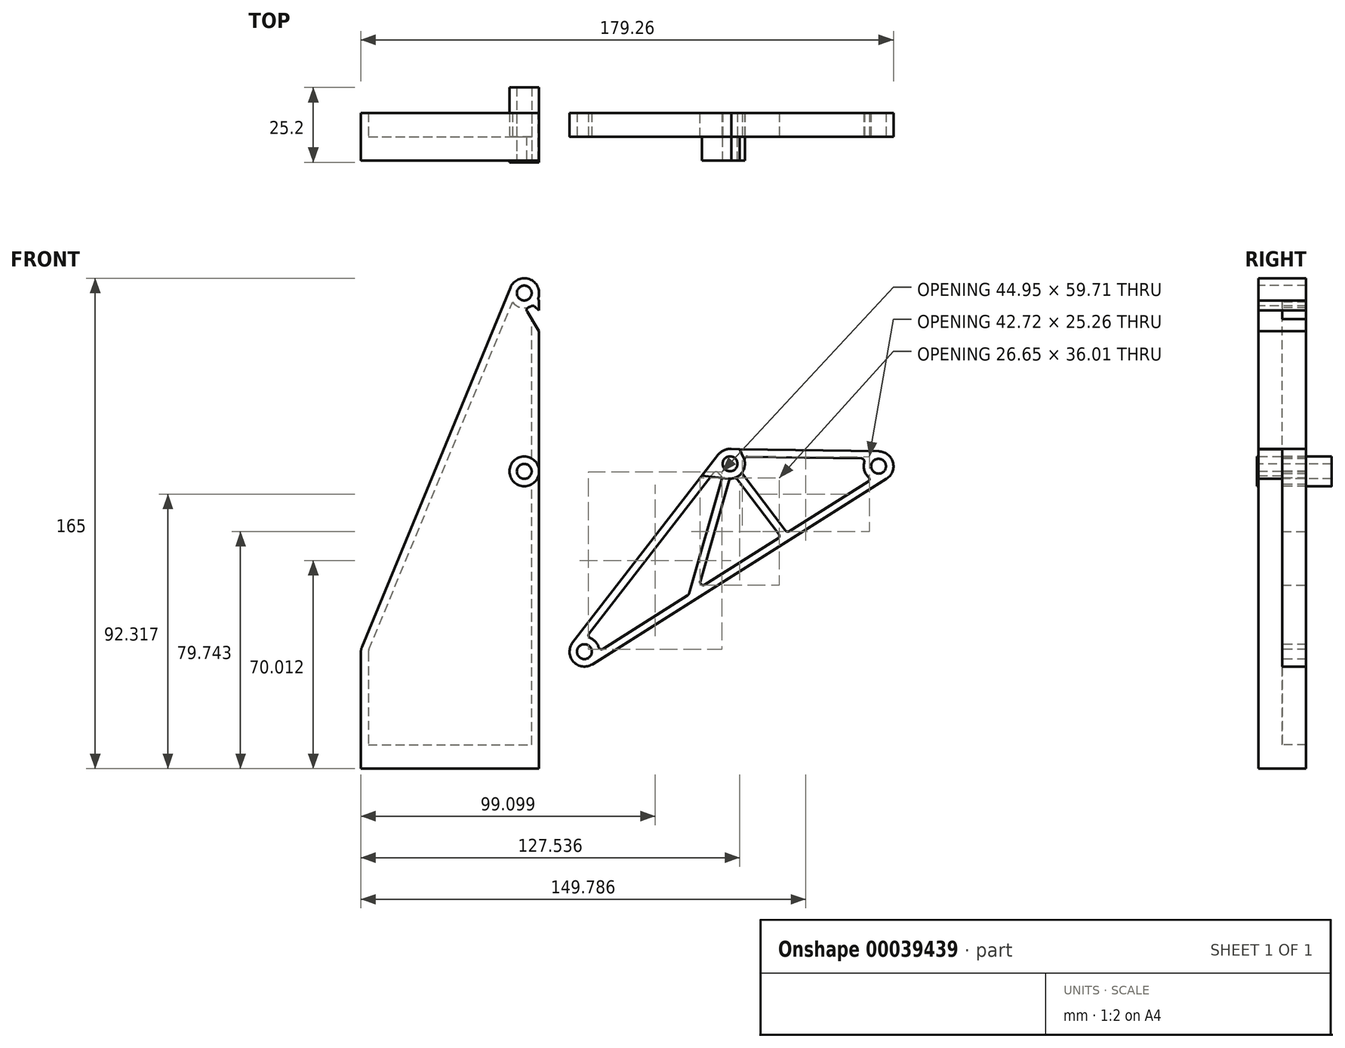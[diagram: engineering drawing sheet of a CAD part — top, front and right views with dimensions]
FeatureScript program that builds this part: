
annotation { "Feature Type Name" : "Feature", "Feature Type Description" : "" }
export const myFeature = defineFeature(function(context is Context, id is Id, definition is map)
    precondition{}
    {
        {
            var Q0;
            Q0=qCreatedBy(makeId("Front.planeOp"),FACE);
            var sketch = newSketch(context, id + "F0", { "sketchPlane" : qUnion([Q0])});
            skLineSegment(sketch, "E0", {"start": v(0, 0) * mm, "end": v(-60, 0) * mm});
            skLineSegment(sketch, "E1", {"start": v(0, 160) * mm, "end": v(0, 0) * mm});
            skCircle(sketch, "E2", {"center": v(-5, 100) * mm, "radius": 2.5 * mm});
            skCircle(sketch, "E3", {"center": v(-5, 160) * mm, "radius": 2.5 * mm});
            skArc(sketch, "E4", {"start": v(0, 160) * mm, "mid": v(-6.37, 164.8) * mm, "end": v(-9.25, 157.36) * mm});
            skLineSegment(sketch, "E5", {"start": v(-5, 160) * mm, "end": v(64.27, 102.54) * mm, "construction": true});
            skLineSegment(sketch, "E6", {"start": v(64.27, 102.54) * mm, "end": v(15.25, 39.32) * mm, "construction": true});
            skLineSegment(sketch, "E7", {"start": v(14.24, 144.04) * mm, "end": v(33.4, 167.13) * mm, "construction": true});
            skLineSegment(sketch, "E8", {"start": v(41.18, 121.7) * mm, "end": v(28.41, 106.3) * mm, "construction": true});
            skLineSegment(sketch, "E9", {"start": v(82.65, 126.25) * mm, "end": v(114.26, 101.74) * mm, "construction": true});
            skLineSegment(sketch, "E10", {"start": v(64.27, 102.54) * mm, "end": v(82.65, 126.25) * mm, "construction": true});
            skArc(sketch, "E11", {"start": v(11.3, 42.38) * mm, "mid": v(11.54, 35.96) * mm, "end": v(17.91, 35.1) * mm});
            skArc(sketch, "E12", {"start": v(116.93, 97.5) * mm, "mid": v(119.08, 103.08) * mm, "end": v(114.34, 106.74) * mm});
            skArc(sketch, "E13", {"start": v(64.35, 107.54) * mm, "mid": v(62.1, 107.05) * mm, "end": v(60.32, 105.6) * mm});
            skLineSegment(sketch, "E14", {"start": v(17.91, 35.1) * mm, "end": v(116.93, 97.5) * mm});
            skLineSegment(sketch, "E15", {"start": v(114.34, 106.74) * mm, "end": v(64.35, 107.54) * mm});
            skLineSegment(sketch, "E16", {"start": v(11.3, 42.38) * mm, "end": v(60.32, 105.6) * mm});
            skArc(sketch, "E17", {"start": v(-5.91, 164.92) * mm, "mid": v(-9.57, 162.02) * mm, "end": v(-9.25, 157.36) * mm});
            skArc(sketch, "E18", {"start": v(37.9, 169.29) * mm, "mid": v(35.66, 171.59) * mm, "end": v(32.48, 172.04) * mm});
            skArc(sketch, "E19", {"start": v(63.75, 97.57) * mm, "mid": v(68.35, 99.66) * mm, "end": v(68.78, 104.7) * mm});
            skArc(sketch, "E20", {"start": v(24.17, 103.66) * mm, "mid": v(25.76, 102.06) * mm, "end": v(27.89, 101.33) * mm});
            skLineSegment(sketch, "E21", {"start": v(24.17, 103.66) * mm, "end": v(-9.25, 157.36) * mm});
            skLineSegment(sketch, "E22", {"start": v(-5.91, 164.92) * mm, "end": v(32.48, 172.04) * mm});
            skLineSegment(sketch, "E23", {"start": v(37.9, 169.29) * mm, "end": v(68.78, 104.7) * mm});
            skLineSegment(sketch, "E24", {"start": v(63.75, 97.57) * mm, "end": v(27.89, 101.33) * mm});
            skCircle(sketch, "E25", {"center": v(33.4, 167.13) * mm, "radius": 2.5 * mm});
            skCircle(sketch, "E26", {"center": v(64.27, 102.54) * mm, "radius": 2.5 * mm});
            skCircle(sketch, "E27", {"center": v(114.26, 101.74) * mm, "radius": 2.5 * mm});
            skCircle(sketch, "E28", {"center": v(15.25, 39.32) * mm, "radius": 2.5 * mm});
            skLineSegment(sketch, "E29", {"start": v(-60, 0) * mm, "end": v(-60, 39) * mm});
            skLineSegment(sketch, "E30", {"start": v(-59.62, 40.92) * mm, "end": v(-9.62, 161.9) * mm});
            skPoint(sketch, "E31.visualSharp", {"position": v(-60, 40) * mm});
            skArc(sketch, "E31.filletArc", {"start": v(-59.62, 40.92) * mm, "mid": v(-59.9, 39.98) * mm, "end": v(-60, 39) * mm});
            skCircle(sketch, "E32", {"center": v(28.41, 106.3) * mm, "radius": 2.5 * mm});
            skPoint(sketch, "E33.endSnap0", {"position": v(-6.37, 164.8) * mm});
            skSolve(sketch);
        }
        {
            var Q0;
            Q0=makeQuery(id+"F0.imprint","IMPRINT",FACE,{"disambiguationData":[TD([[makeQuery(id+"F0.imprint","IMPRINT",EDGE,{"derivedFrom":sQuery(id+"F0.wireOp",EDGE,"E0")}),-1.0]])]});
            var Q1;
            Q1=makeQuery(id+"F0.imprint","IMPRINT",FACE,{"disambiguationData":[TD([[makeQuery(id+"F0.imprint","IMPRINT",EDGE,{"derivedFrom":sQuery(id+"F0.wireOp",EDGE,"E3")}),-1.0]])]});
            extrude(context, id + "F1", {"entities" : qUnion([Q0, Q1]), "oppositeDirection" : true, "depth" : 8 * mm});
        }
        {
            var Q0;
            {var subQ7=sQuery(id+"F0.wireOp",EDGE,"E4");Q0=makeQuery(id+"F0.imprint","IMPRINT",FACE,{"disambiguationData":[TD([[makeQuery(id+"F0.imprint","IMPRINT",EDGE,{"derivedFrom":subQ7}),-1.0]])]});}
            var Q1;
            {var subQ4=sQuery(id+"F0.wireOp",EDGE,"E13");Q1=makeQuery(id+"F0.imprint","IMPRINT",FACE,{"disambiguationData":[TD([[makeQuery(id+"F0.imprint","IMPRINT",EDGE,{"derivedFrom":subQ4}),1.0]])]});}
            var Q2;
            Q2=makeQuery(id+"F0.imprint","IMPRINT",FACE,{"disambiguationData":[TD([[makeQuery(id+"F0.imprint","IMPRINT",EDGE,{"derivedFrom":sQuery(id+"F0.wireOp",EDGE,"E3")}),-1.0]])]});
            extrude(context, id + "F2", {"entities" : qUnion([Q0, Q1, Q2]), "depth" : 8 * mm});
        }
        {
            var Q0;
            {var subQ3=sQuery(id+"F0.wireOp",EDGE,"E11");Q0=makeQuery(id+"F0.imprint","IMPRINT",FACE,{"disambiguationData":[TD([[makeQuery(id+"F0.imprint","IMPRINT",EDGE,{"derivedFrom":subQ3}),1.0]])]});}
            var Q1;
            {var subQ4=sQuery(id+"F0.wireOp",EDGE,"E13");Q1=makeQuery(id+"F0.imprint","IMPRINT",FACE,{"disambiguationData":[TD([[makeQuery(id+"F0.imprint","IMPRINT",EDGE,{"derivedFrom":subQ4}),1.0]])]});}
            var Q2;
            {var subQ0=sQuery(id+"F0.wireOp",EDGE,"E12");Q2=makeQuery(id+"F0.imprint","IMPRINT",FACE,{"disambiguationData":[TD([[makeQuery(id+"F0.imprint","IMPRINT",EDGE,{"derivedFrom":subQ0}),1.0]])]});}
            extrude(context, id + "F3", {"entities" : qUnion([Q0, Q1, Q2]), "oppositeDirection" : true, "depth" : 8 * mm});
        }
        {
            var Q0;
            Q0=makeQuery(id+"F3.opExtrude","CAP_FACE",FACE,{"disambiguationData":[OSD([sQuery(id+"F0.wireOp",EDGE,"E11"),sQuery(id+"F0.wireOp",EDGE,"E12"),sQuery(id+"F0.wireOp",EDGE,"E13"),sQuery(id+"F0.wireOp",EDGE,"E14"),sQuery(id+"F0.wireOp",EDGE,"E15"),sQuery(id+"F0.wireOp",EDGE,"E16"),sQuery(id+"F0.wireOp",EDGE,"E26"),sQuery(id+"F0.wireOp",EDGE,"E27"),sQuery(id+"F0.wireOp",EDGE,"E28")])],"isStart":true});
            var sketch = newSketch(context, id + "F4", { "sketchPlane" : qUnion([Q0])});
            skLineSegment(sketch, "E34.0", {"start": v(13.27, 40.85) * mm, "end": v(15.92, 44.27) * mm});
            skLineSegment(sketch, "E35.0", {"start": v(114.3, 104.24) * mm, "end": v(64.31, 105.04) * mm});
            skLineSegment(sketch, "E36.0", {"start": v(16.58, 37.2) * mm, "end": v(20.24, 39.51) * mm});
            skCircle(sketch, "E37", {"center": v(114.26, 101.74) * mm, "radius": 2.5 * mm});
            skCircle(sketch, "E38", {"center": v(15.25, 39.32) * mm, "radius": 2.5 * mm});
            skArc(sketch, "E39", {"start": v(20.24, 39.51) * mm, "mid": v(18.95, 42.68) * mm, "end": v(15.92, 44.27) * mm});
            skLineSegment(sketch, "E40.trimOffspring", {"start": v(20.24, 39.51) * mm, "end": v(115.6, 99.62) * mm});
            skLineSegment(sketch, "E41.trimOffspring", {"start": v(15.92, 44.27) * mm, "end": v(62.3, 104.07) * mm});
            skCircle(sketch, "E42", {"center": v(114.26, 101.74) * mm, "radius": 5 * mm});
            skCircle(sketch, "E43", {"center": v(64.27, 102.54) * mm, "radius": 5 * mm});
            skLineSegment(sketch, "E44", {"start": v(64.27, 102.54) * mm, "end": v(50.9, 55.89) * mm, "construction": true});
            skLineSegment(sketch, "E45", {"start": v(64.27, 102.54) * mm, "end": v(83.9, 76.68) * mm, "construction": true});
            skLineSegment(sketch, "E46", {"start": v(115.6, 99.62) * mm, "end": v(116.93, 97.5) * mm, "construction": true});
            skLineSegment(sketch, "E47.0", {"start": v(63.07, 102.88) * mm, "end": v(49.7, 56.23) * mm});
            skLineSegment(sketch, "E48.0", {"start": v(65.47, 102.2) * mm, "end": v(52.1, 55.54) * mm});
            skLineSegment(sketch, "E49.0", {"start": v(63.27, 101.78) * mm, "end": v(82.9, 75.93) * mm});
            skLineSegment(sketch, "E50.0", {"start": v(65.27, 103.3) * mm, "end": v(84.9, 77.44) * mm});
            skSolve(sketch);
        }
        {
            var Q0;
            {var subQ8=sQuery(id+"F4.wireOp",EDGE,"e6ad8ed1-898a-40d8-b4cc-a0c7f3deb401");Q0=makeQuery(id+"F4.imprint","IMPRINT",FACE,{"disambiguationData":[TD([[makeQuery(id+"F4.imprint","IMPRINT",EDGE,{"derivedFrom":subQ8}),-1.0]])]});}
            var Q1;
            {var subQ4=sQuery(id+"F4.wireOp",EDGE,"71649f5b-346c-4b52-ad70-852c755155e4");Q1=makeQuery(id+"F4.imprint","IMPRINT",FACE,{"disambiguationData":[TD([[makeQuery(id+"F4.imprint","IMPRINT",EDGE,{"derivedFrom":subQ4}),1.0]])]});}
            var Q2;
            {var subQ5=sQuery(id+"F4.wireOp",EDGE,"E39");Q2=makeQuery(id+"F4.imprint","IMPRINT",FACE,{"disambiguationData":[TD([[makeQuery(id+"F4.imprint","IMPRINT",EDGE,{"derivedFrom":subQ5}),-1.0]])]});}
            var Q3;
            {var subQ7=sQuery(id+"F4.wireOp",EDGE,"cc853d74-6e0b-4ffd-9b44-5db66f43a1f3");Q3=makeQuery(id+"F4.imprint","IMPRINT",FACE,{"disambiguationData":[TD([[makeQuery(id+"F4.imprint","IMPRINT",EDGE,{"derivedFrom":subQ7}),1.0]])]});}
            var Q4;
            {var subQ3=sQuery(id+"F4.wireOp",EDGE,"E40.trimOffspring");var subQ5=sQuery(id+"F4.wireOp",EDGE,"E48.0");var subQ7=makeQuery(id+"F4.imprint","INTERSECT",VERTEX,{"derivedFrom":[subQ3,subQ5]});Q4=makeQuery(id+"F4.imprint","IMPRINT",FACE,{"disambiguationData":[TD([[makeQuery(id+"F4.imprint","IMPRINT",EDGE,{"disambiguationData":[TD([[subQ7,-1.0]])],"derivedFrom":subQ3}),1.0]])]});}
            var Q5;
            {var subQ5=sQuery(id+"F4.wireOp",EDGE,"E35.0");var subQ7=sQuery(id+"F4.wireOp",EDGE,"E42");var subQ8=makeQuery(id+"F4.imprint","INTERSECT",VERTEX,{"derivedFrom":[subQ5,subQ7]});Q5=makeQuery(id+"F4.imprint","IMPRINT",FACE,{"disambiguationData":[TD([[makeQuery(id+"F4.imprint","IMPRINT",EDGE,{"disambiguationData":[TD([[subQ8,-1.0]])],"derivedFrom":subQ5}),1.0]])]});}
            extrude(context, id + "F5", {"entities" : qUnion([Q0, Q1, Q2, Q3, Q4, Q5]), "operationType" : NewBodyOperationType.REMOVE, "endBound" : BoundingType.THROUGH_ALL, "oppositeDirection" : true, "depth" : 25 * mm});
        }
        {
            var Q0;
            Q0=makeQuery(id+"F2.opExtrude","CAP_FACE",FACE,{"disambiguationData":[OSD([sQuery(id+"F0.wireOp",EDGE,"E3"),sQuery(id+"F0.wireOp",EDGE,"E17"),sQuery(id+"F0.wireOp",EDGE,"E18"),sQuery(id+"F0.wireOp",EDGE,"E19"),sQuery(id+"F0.wireOp",EDGE,"E20"),sQuery(id+"F0.wireOp",EDGE,"E21"),sQuery(id+"F0.wireOp",EDGE,"E22"),sQuery(id+"F0.wireOp",EDGE,"E23"),sQuery(id+"F0.wireOp",EDGE,"E24"),sQuery(id+"F0.wireOp",EDGE,"E25"),sQuery(id+"F0.wireOp",EDGE,"E26"),sQuery(id+"F0.wireOp",EDGE,"E32")])],"isStart":false});
            var sketch = newSketch(context, id + "F6", { "sketchPlane" : qUnion([Q0])});
            skLineSegment(sketch, "E51", {"start": v(28.41, 106.3) * mm, "end": v(33.4, 167.13) * mm, "construction": true});
            skLineSegment(sketch, "E52", {"start": v(-5, 160) * mm, "end": v(64.27, 102.54) * mm, "construction": true});
            skLineSegment(sketch, "E53.0", {"start": v(-5.46, 162.46) * mm, "end": v(32.94, 169.59) * mm});
            skLineSegment(sketch, "E54", {"start": v(-7.12, 158.68) * mm, "end": v(26.29, 104.98) * mm});
            skLineSegment(sketch, "E55", {"start": v(28.15, 103.81) * mm, "end": v(64, 100.05) * mm});
            skLineSegment(sketch, "E56", {"start": v(66.53, 103.62) * mm, "end": v(35.65, 168.2) * mm});
            skCircle(sketch, "E57", {"center": v(-5, 160) * mm, "radius": 5 * mm});
            skCircle(sketch, "E58", {"center": v(33.4, 167.13) * mm, "radius": 5 * mm});
            skCircle(sketch, "E59", {"center": v(64.27, 102.54) * mm, "radius": 5 * mm});
            skCircle(sketch, "E60", {"center": v(28.41, 106.3) * mm, "radius": 5 * mm});
            skLineSegment(sketch, "E61.0", {"start": v(29.66, 106.2) * mm, "end": v(34.64, 167.03) * mm});
            skLineSegment(sketch, "E62.0", {"start": v(27.17, 106.4) * mm, "end": v(32.15, 167.23) * mm});
            skLineSegment(sketch, "E63.0", {"start": v(-5.8, 159.04) * mm, "end": v(63.47, 101.58) * mm});
            skLineSegment(sketch, "E64.0", {"start": v(-4.2, 160.96) * mm, "end": v(65.07, 103.5) * mm});
            skSolve(sketch);
        }
        {
            var Q0;
            {var subQ3=sQuery(id+"F6.wireOp",EDGE,"E57");var subQ7=sQuery(id+"F6.wireOp",EDGE,"E54");var subQ9=makeQuery(id+"F6.imprint","INTERSECT",VERTEX,{"derivedFrom":[subQ7,subQ3]});Q0=makeQuery(id+"F6.imprint","IMPRINT",FACE,{"disambiguationData":[TD([[makeQuery(id+"F6.imprint","IMPRINT",EDGE,{"disambiguationData":[TD([[subQ9,-1.0]])],"derivedFrom":subQ7}),1.0]])]});}
            var Q1;
            {var subQ3=sQuery(id+"F6.wireOp",EDGE,"E57");var subQ5=sQuery(id+"F6.wireOp",EDGE,"E53.0");var subQ8=makeQuery(id+"F6.imprint","INTERSECT",VERTEX,{"derivedFrom":[subQ5,subQ3]});Q1=makeQuery(id+"F6.imprint","IMPRINT",FACE,{"disambiguationData":[TD([[makeQuery(id+"F6.imprint","IMPRINT",EDGE,{"disambiguationData":[TD([[subQ8,-1.0]])],"derivedFrom":subQ5}),-1.0]])]});}
            var Q2;
            {var subQ3=sQuery(id+"F6.wireOp",EDGE,"E59");var subQ5=sQuery(id+"F6.wireOp",EDGE,"E56");var subQ8=makeQuery(id+"F6.imprint","INTERSECT",VERTEX,{"derivedFrom":[subQ5,subQ3]});Q2=makeQuery(id+"F6.imprint","IMPRINT",FACE,{"disambiguationData":[TD([[makeQuery(id+"F6.imprint","IMPRINT",EDGE,{"disambiguationData":[TD([[subQ8,-1.0]])],"derivedFrom":subQ5}),1.0]])]});}
            var Q3;
            {var subQ5=sQuery(id+"F6.wireOp",EDGE,"E60");var subQ7=sQuery(id+"F6.wireOp",EDGE,"E55");var subQ8=makeQuery(id+"F6.imprint","INTERSECT",VERTEX,{"derivedFrom":[subQ7,subQ5]});Q3=makeQuery(id+"F6.imprint","IMPRINT",FACE,{"disambiguationData":[TD([[makeQuery(id+"F6.imprint","IMPRINT",EDGE,{"disambiguationData":[TD([[subQ8,-1.0]])],"derivedFrom":subQ7}),1.0]])]});}
            extrude(context, id + "F7", {"entities" : qUnion([Q0, Q1, Q2, Q3]), "operationType" : NewBodyOperationType.REMOVE, "endBound" : BoundingType.THROUGH_ALL, "oppositeDirection" : true, "depth" : 25 * mm});
        }
        {
            var Q0;
            Q0=makeQuery(id+"F7.boolean.opBoolean","COPY",EDGE,{"derivedFrom":makeQuery(id+"F7.opExtrude","SWEPT_EDGE",EDGE,{"disambiguationData":[OSD([sQuery(id+"F6.wireOp",EDGE,"E57"),sQuery(id+"F6.wireOp",EDGE,"E63.0")])]})});
            var Q1;
            Q1=makeQuery(id+"F7.boolean.opBoolean","COPY",EDGE,{"derivedFrom":makeQuery(id+"F7.opExtrude","SWEPT_EDGE",EDGE,{"disambiguationData":[OSD([sQuery(id+"F6.wireOp",EDGE,"E54"),sQuery(id+"F6.wireOp",EDGE,"E57")])]})});
            var Q2;
            Q2=makeQuery(id+"F7.boolean.opBoolean","COPY",EDGE,{"derivedFrom":makeQuery(id+"F7.opExtrude","SWEPT_EDGE",EDGE,{"disambiguationData":[OSD([sQuery(id+"F6.wireOp",EDGE,"E57"),sQuery(id+"F6.wireOp",EDGE,"E64.0")])]})});
            var Q3;
            Q3=makeQuery(id+"F7.boolean.opBoolean","COPY",EDGE,{"derivedFrom":makeQuery(id+"F7.opExtrude","SWEPT_EDGE",EDGE,{"disambiguationData":[OSD([sQuery(id+"F6.wireOp",EDGE,"E53.0"),sQuery(id+"F6.wireOp",EDGE,"E57")])]})});
            var Q4;
            Q4=makeQuery(id+"F7.boolean.opBoolean","COPY",EDGE,{"derivedFrom":makeQuery(id+"F7.opExtrude","SWEPT_EDGE",EDGE,{"disambiguationData":[OSD([sQuery(id+"F6.wireOp",EDGE,"E53.0"),sQuery(id+"F6.wireOp",EDGE,"E58")])]})});
            var Q5;
            Q5=makeQuery(id+"F7.boolean.opBoolean","COPY",EDGE,{"derivedFrom":makeQuery(id+"F7.opExtrude","SWEPT_EDGE",EDGE,{"disambiguationData":[OSD([sQuery(id+"F6.wireOp",EDGE,"E58"),sQuery(id+"F6.wireOp",EDGE,"E62.0")])]})});
            var Q6;
            Q6=makeQuery(id+"F7.boolean.opBoolean","COPY",EDGE,{"derivedFrom":makeQuery(id+"F7.opExtrude","SWEPT_EDGE",EDGE,{"disambiguationData":[OSD([sQuery(id+"F6.wireOp",EDGE,"E58"),sQuery(id+"F6.wireOp",EDGE,"E61.0")])]})});
            var Q7;
            Q7=makeQuery(id+"F7.boolean.opBoolean","COPY",EDGE,{"derivedFrom":makeQuery(id+"F7.opExtrude","SWEPT_EDGE",EDGE,{"disambiguationData":[OSD([sQuery(id+"F6.wireOp",EDGE,"E56"),sQuery(id+"F6.wireOp",EDGE,"E58")])]})});
            var Q8;
            Q8=makeQuery(id+"F7.boolean.opBoolean","COPY",EDGE,{"derivedFrom":makeQuery(id+"F7.opExtrude","SWEPT_EDGE",EDGE,{"disambiguationData":[OSD([sQuery(id+"F6.wireOp",EDGE,"E62.0"),sQuery(id+"F6.wireOp",EDGE,"E64.0")])]})});
            var Q9;
            Q9=makeQuery(id+"F7.boolean.opBoolean","COPY",EDGE,{"derivedFrom":makeQuery(id+"F7.opExtrude","SWEPT_EDGE",EDGE,{"disambiguationData":[OSD([sQuery(id+"F6.wireOp",EDGE,"E62.0"),sQuery(id+"F6.wireOp",EDGE,"E63.0")])]})});
            var Q10;
            Q10=makeQuery(id+"F7.boolean.opBoolean","COPY",EDGE,{"derivedFrom":makeQuery(id+"F7.opExtrude","SWEPT_EDGE",EDGE,{"disambiguationData":[OSD([sQuery(id+"F6.wireOp",EDGE,"E61.0"),sQuery(id+"F6.wireOp",EDGE,"E63.0")])]})});
            var Q11;
            Q11=makeQuery(id+"F7.boolean.opBoolean","COPY",EDGE,{"derivedFrom":makeQuery(id+"F7.opExtrude","SWEPT_EDGE",EDGE,{"disambiguationData":[OSD([sQuery(id+"F6.wireOp",EDGE,"E61.0"),sQuery(id+"F6.wireOp",EDGE,"E64.0")])]})});
            var Q12;
            Q12=makeQuery(id+"F7.boolean.opBoolean","COPY",EDGE,{"derivedFrom":makeQuery(id+"F7.opExtrude","SWEPT_EDGE",EDGE,{"disambiguationData":[OSD([sQuery(id+"F6.wireOp",EDGE,"E60"),sQuery(id+"F6.wireOp",EDGE,"E62.0")])]})});
            var Q13;
            Q13=makeQuery(id+"F7.boolean.opBoolean","COPY",EDGE,{"derivedFrom":makeQuery(id+"F7.opExtrude","SWEPT_EDGE",EDGE,{"disambiguationData":[OSD([sQuery(id+"F6.wireOp",EDGE,"E54"),sQuery(id+"F6.wireOp",EDGE,"E60")])]})});
            var Q14;
            Q14=makeQuery(id+"F7.boolean.opBoolean","COPY",EDGE,{"derivedFrom":makeQuery(id+"F7.opExtrude","SWEPT_EDGE",EDGE,{"disambiguationData":[OSD([sQuery(id+"F6.wireOp",EDGE,"E60"),sQuery(id+"F6.wireOp",EDGE,"E61.0")])]})});
            var Q15;
            Q15=makeQuery(id+"F7.boolean.opBoolean","COPY",EDGE,{"derivedFrom":makeQuery(id+"F7.opExtrude","SWEPT_EDGE",EDGE,{"disambiguationData":[OSD([sQuery(id+"F6.wireOp",EDGE,"E55"),sQuery(id+"F6.wireOp",EDGE,"E60")])]})});
            var Q16;
            Q16=makeQuery(id+"F7.boolean.opBoolean","COPY",EDGE,{"derivedFrom":makeQuery(id+"F7.opExtrude","SWEPT_EDGE",EDGE,{"disambiguationData":[OSD([sQuery(id+"F6.wireOp",EDGE,"E55"),sQuery(id+"F6.wireOp",EDGE,"E59")])]})});
            var Q17;
            Q17=makeQuery(id+"F7.boolean.opBoolean","COPY",EDGE,{"derivedFrom":makeQuery(id+"F7.opExtrude","SWEPT_EDGE",EDGE,{"disambiguationData":[OSD([sQuery(id+"F6.wireOp",EDGE,"E59"),sQuery(id+"F6.wireOp",EDGE,"E63.0")])]})});
            var Q18;
            Q18=makeQuery(id+"F7.boolean.opBoolean","COPY",EDGE,{"derivedFrom":makeQuery(id+"F7.opExtrude","SWEPT_EDGE",EDGE,{"disambiguationData":[OSD([sQuery(id+"F6.wireOp",EDGE,"E59"),sQuery(id+"F6.wireOp",EDGE,"E64.0")])]})});
            var Q19;
            Q19=makeQuery(id+"F7.boolean.opBoolean","COPY",EDGE,{"derivedFrom":makeQuery(id+"F7.opExtrude","SWEPT_EDGE",EDGE,{"disambiguationData":[OSD([sQuery(id+"F6.wireOp",EDGE,"E56"),sQuery(id+"F6.wireOp",EDGE,"E59")])]})});
            fillet(context, id + "F8", {"entities" : qUnion([Q0, Q1, Q2, Q3, Q4, Q5, Q6, Q7, Q8, Q9, Q10, Q11, Q12, Q13, Q14, Q15, Q16, Q17, Q18, Q19]), "radius" : 1 * mm, "tangentPropagation" : true, "allowEdgeOverflow" : false});
        }
        {
            var Q0;
            Q0=makeQuery(id+"F5.boolean.opBoolean","COPY",EDGE,{"derivedFrom":makeQuery(id+"F5.opExtrude","SWEPT_EDGE",EDGE,{"disambiguationData":[OSD([sQuery(id+"F4.wireOp",EDGE,"E34.0"),sQuery(id+"F4.wireOp",EDGE,"E39"),sQuery(id+"F4.wireOp",EDGE,"E41.trimOffspring")])]})});
            var Q1;
            Q1=makeQuery(id+"F5.boolean.opBoolean","COPY",EDGE,{"derivedFrom":makeQuery(id+"F5.opExtrude","SWEPT_EDGE",EDGE,{"disambiguationData":[OSD([sQuery(id+"F4.wireOp",EDGE,"E36.0"),sQuery(id+"F4.wireOp",EDGE,"E39"),sQuery(id+"F4.wireOp",EDGE,"E40.trimOffspring")])]})});
            var Q2;
            Q2=makeQuery(id+"F5.boolean.opBoolean","COPY",EDGE,{"derivedFrom":makeQuery(id+"F5.opExtrude","SWEPT_EDGE",EDGE,{"disambiguationData":[OSD([sQuery(id+"F4.wireOp",EDGE,"E41.trimOffspring"),sQuery(id+"F4.wireOp",EDGE,"0e49a260-5e05-47f3-8dac-0c4ef003415c")])]})});
            var Q3;
            Q3=makeQuery(id+"F5.boolean.opBoolean","COPY",EDGE,{"derivedFrom":makeQuery(id+"F5.opExtrude","SWEPT_EDGE",EDGE,{"disambiguationData":[OSD([sQuery(id+"F4.wireOp",EDGE,"b29edf23-7984-4d3a-8bd0-73782f2ce4bf"),sQuery(id+"F4.wireOp",EDGE,"0e49a260-5e05-47f3-8dac-0c4ef003415c")])]})});
            var Q4;
            Q4=makeQuery(id+"F5.boolean.opBoolean","COPY",EDGE,{"derivedFrom":makeQuery(id+"F5.opExtrude","SWEPT_EDGE",EDGE,{"disambiguationData":[OSD([sQuery(id+"F4.wireOp",EDGE,"cc853d74-6e0b-4ffd-9b44-5db66f43a1f3"),sQuery(id+"F4.wireOp",EDGE,"0e49a260-5e05-47f3-8dac-0c4ef003415c")])]})});
            var Q5;
            Q5=makeQuery(id+"F5.boolean.opBoolean","COPY",EDGE,{"derivedFrom":makeQuery(id+"F5.opExtrude","SWEPT_EDGE",EDGE,{"disambiguationData":[OSD([sQuery(id+"F4.wireOp",EDGE,"E35.0"),sQuery(id+"F4.wireOp",EDGE,"0e49a260-5e05-47f3-8dac-0c4ef003415c")])]})});
            var Q6;
            Q6=makeQuery(id+"F5.boolean.opBoolean","COPY",EDGE,{"derivedFrom":makeQuery(id+"F5.opExtrude","SWEPT_EDGE",EDGE,{"disambiguationData":[OSD([sQuery(id+"F4.wireOp",EDGE,"E40.trimOffspring"),sQuery(id+"F4.wireOp",EDGE,"b29edf23-7984-4d3a-8bd0-73782f2ce4bf")])]})});
            var Q7;
            Q7=makeQuery(id+"F5.boolean.opBoolean","COPY",EDGE,{"derivedFrom":makeQuery(id+"F5.opExtrude","SWEPT_EDGE",EDGE,{"disambiguationData":[OSD([sQuery(id+"F4.wireOp",EDGE,"E40.trimOffspring"),sQuery(id+"F4.wireOp",EDGE,"cc853d74-6e0b-4ffd-9b44-5db66f43a1f3")])]})});
            var Q8;
            Q8=makeQuery(id+"F5.boolean.opBoolean","COPY",EDGE,{"derivedFrom":makeQuery(id+"F5.opExtrude","SWEPT_EDGE",EDGE,{"disambiguationData":[OSD([sQuery(id+"F4.wireOp",EDGE,"E40.trimOffspring"),sQuery(id+"F4.wireOp",EDGE,"E42")])]})});
            var Q9;
            Q9=makeQuery(id+"F5.boolean.opBoolean","COPY",EDGE,{"derivedFrom":makeQuery(id+"F5.opExtrude","SWEPT_EDGE",EDGE,{"disambiguationData":[OSD([sQuery(id+"F4.wireOp",EDGE,"E35.0"),sQuery(id+"F4.wireOp",EDGE,"E42")])]})});
            var Q10;
            Q10=makeQuery(id+"F5.boolean.opBoolean","COPY",EDGE,{"derivedFrom":makeQuery(id+"F5.opExtrude","SWEPT_EDGE",EDGE,{"disambiguationData":[OSD([sQuery(id+"F4.wireOp",EDGE,"E43"),sQuery(id+"F4.wireOp",EDGE,"E50.0")])]})});
            var Q11;
            Q11=makeQuery(id+"F5.boolean.opBoolean","COPY",EDGE,{"derivedFrom":makeQuery(id+"F5.opExtrude","SWEPT_EDGE",EDGE,{"disambiguationData":[OSD([sQuery(id+"F4.wireOp",EDGE,"E43"),sQuery(id+"F4.wireOp",EDGE,"E49.0")])]})});
            var Q12;
            Q12=makeQuery(id+"F5.boolean.opBoolean","COPY",EDGE,{"derivedFrom":makeQuery(id+"F5.opExtrude","SWEPT_EDGE",EDGE,{"disambiguationData":[OSD([sQuery(id+"F4.wireOp",EDGE,"E43"),sQuery(id+"F4.wireOp",EDGE,"E48.0")])]})});
            var Q13;
            Q13=makeQuery(id+"F5.boolean.opBoolean","COPY",EDGE,{"derivedFrom":makeQuery(id+"F5.opExtrude","SWEPT_EDGE",EDGE,{"disambiguationData":[OSD([sQuery(id+"F4.wireOp",EDGE,"E43"),sQuery(id+"F4.wireOp",EDGE,"E47.0")])]})});
            fillet(context, id + "F9", {"entities" : qUnion([Q0, Q1, Q2, Q3, Q4, Q5, Q6, Q7, Q8, Q9, Q10, Q11, Q12, Q13]), "radius" : 1 * mm, "tangentPropagation" : true, "allowEdgeOverflow" : false});
        }
        {
            var Q0;
            Q0=makeQuery(id+"F1.opExtrude","CAP_FACE",FACE,{"disambiguationData":[OSD([sQuery(id+"F0.wireOp",EDGE,"E0"),sQuery(id+"F0.wireOp",EDGE,"E1"),sQuery(id+"F0.wireOp",EDGE,"E2"),sQuery(id+"F0.wireOp",EDGE,"E3"),sQuery(id+"F0.wireOp",EDGE,"E4"),sQuery(id+"F0.wireOp",EDGE,"E17"),sQuery(id+"F0.wireOp",EDGE,"E29"),sQuery(id+"F0.wireOp",EDGE,"E30"),sQuery(id+"F0.wireOp",EDGE,"E31.filletArc")])],"isStart":true});
            var sketch = newSketch(context, id + "F10", { "sketchPlane" : qUnion([Q0])});
            skCircle(sketch, "E65", {"center": v(-5, 160) * mm, "radius": 5 * mm});
            skLineSegment(sketch, "E66", {"start": v(-2.5, 0) * mm, "end": v(-2.5, 160) * mm});
            skLineSegment(sketch, "E67", {"start": v(-57.31, 39.96) * mm, "end": v(-7.31, 160.95) * mm});
            skArc(sketch, "E68", {"start": v(-57.31, 39.96) * mm, "mid": v(-57.45, 39.5) * mm, "end": v(-57.5, 39) * mm});
            skLineSegment(sketch, "E69", {"start": v(-57.5, 39) * mm, "end": v(-57.5, 0) * mm});
            skCircle(sketch, "E70", {"center": v(-5, 100) * mm, "radius": 5 * mm});
            skLineSegment(sketch, "E71", {"start": v(-57.5, 8) * mm, "end": v(-2.5, 8) * mm});
            skSolve(sketch);
        }
        {
            var Q0;
            {var subQ5=sQuery(id+"F10.wireOp",EDGE,"E68");Q0=makeQuery(id+"F10.imprint","IMPRINT",FACE,{"disambiguationData":[TD([[makeQuery(id+"F10.imprint","IMPRINT",EDGE,{"derivedFrom":subQ5}),1.0]])]});}
            extrude(context, id + "F11", {"entities" : qUnion([Q0]), "operationType" : NewBodyOperationType.REMOVE, "endBound" : BoundingType.THROUGH_ALL, "oppositeDirection" : true, "depth" : 25 * mm});
        }
        {
            var Q0;
            Q0=makeQuery(id+"F1.opExtrude","CAP_FACE",FACE,{"disambiguationData":[OSD([sQuery(id+"F0.wireOp",EDGE,"E0"),sQuery(id+"F0.wireOp",EDGE,"E1"),sQuery(id+"F0.wireOp",EDGE,"E2"),sQuery(id+"F0.wireOp",EDGE,"E3"),sQuery(id+"F0.wireOp",EDGE,"E4"),sQuery(id+"F0.wireOp",EDGE,"E17"),sQuery(id+"F0.wireOp",EDGE,"E29"),sQuery(id+"F0.wireOp",EDGE,"E30"),sQuery(id+"F0.wireOp",EDGE,"E31.filletArc")])],"isStart":true});
            var sketch = newSketch(context, id + "F12", { "sketchPlane" : qUnion([Q0])});
            skCircle(sketch, "E72.0", {"center": v(-5, 100) * mm, "radius": 2.5 * mm});
            skCircle(sketch, "E73", {"center": v(-5, 100) * mm, "radius": 5 * mm});
            skSolve(sketch);
        }
        {
            var Q0;
            Q0=makeQuery(id+"F12.imprint","IMPRINT",FACE,{"disambiguationData":[TD([[makeQuery(id+"F12.imprint","IMPRINT",EDGE,{"derivedFrom":sQuery(id+"F12.wireOp",EDGE,"E72.0")}),-1.0]])]});
            extrude(context, id + "F13", {"entities" : qUnion([Q0]), "operationType" : NewBodyOperationType.ADD, "depth" : 8.6 * mm});
        }
        {
            var Q0;
            Q0=makeQuery(id+"F1.opExtrude","CAP_FACE",FACE,{"disambiguationData":[OSD([sQuery(id+"F0.wireOp",EDGE,"E0"),sQuery(id+"F0.wireOp",EDGE,"E1"),sQuery(id+"F0.wireOp",EDGE,"E2"),sQuery(id+"F0.wireOp",EDGE,"E3"),sQuery(id+"F0.wireOp",EDGE,"E4"),sQuery(id+"F0.wireOp",EDGE,"E17"),sQuery(id+"F0.wireOp",EDGE,"E29"),sQuery(id+"F0.wireOp",EDGE,"E30"),sQuery(id+"F0.wireOp",EDGE,"E31.filletArc")])],"isStart":false});
            var sketch = newSketch(context, id + "F14", { "sketchPlane" : qUnion([Q0])});
            skCircle(sketch, "E74.0", {"center": v(5, 100) * mm, "radius": 2.5 * mm});
            skCircle(sketch, "E75", {"center": v(5, 100) * mm, "radius": 5 * mm});
            skSolve(sketch);
        }
        {
            var Q0;
            Q0=makeQuery(id+"F14.imprint","IMPRINT",FACE,{"disambiguationData":[TD([[makeQuery(id+"F14.imprint","IMPRINT",EDGE,{"derivedFrom":sQuery(id+"F14.wireOp",EDGE,"E74.0")}),1.0]])]});
            extrude(context, id + "F15", {"entities" : qUnion([Q0]), "operationType" : NewBodyOperationType.ADD, "depth" : 8.6 * mm});
        }
    });
